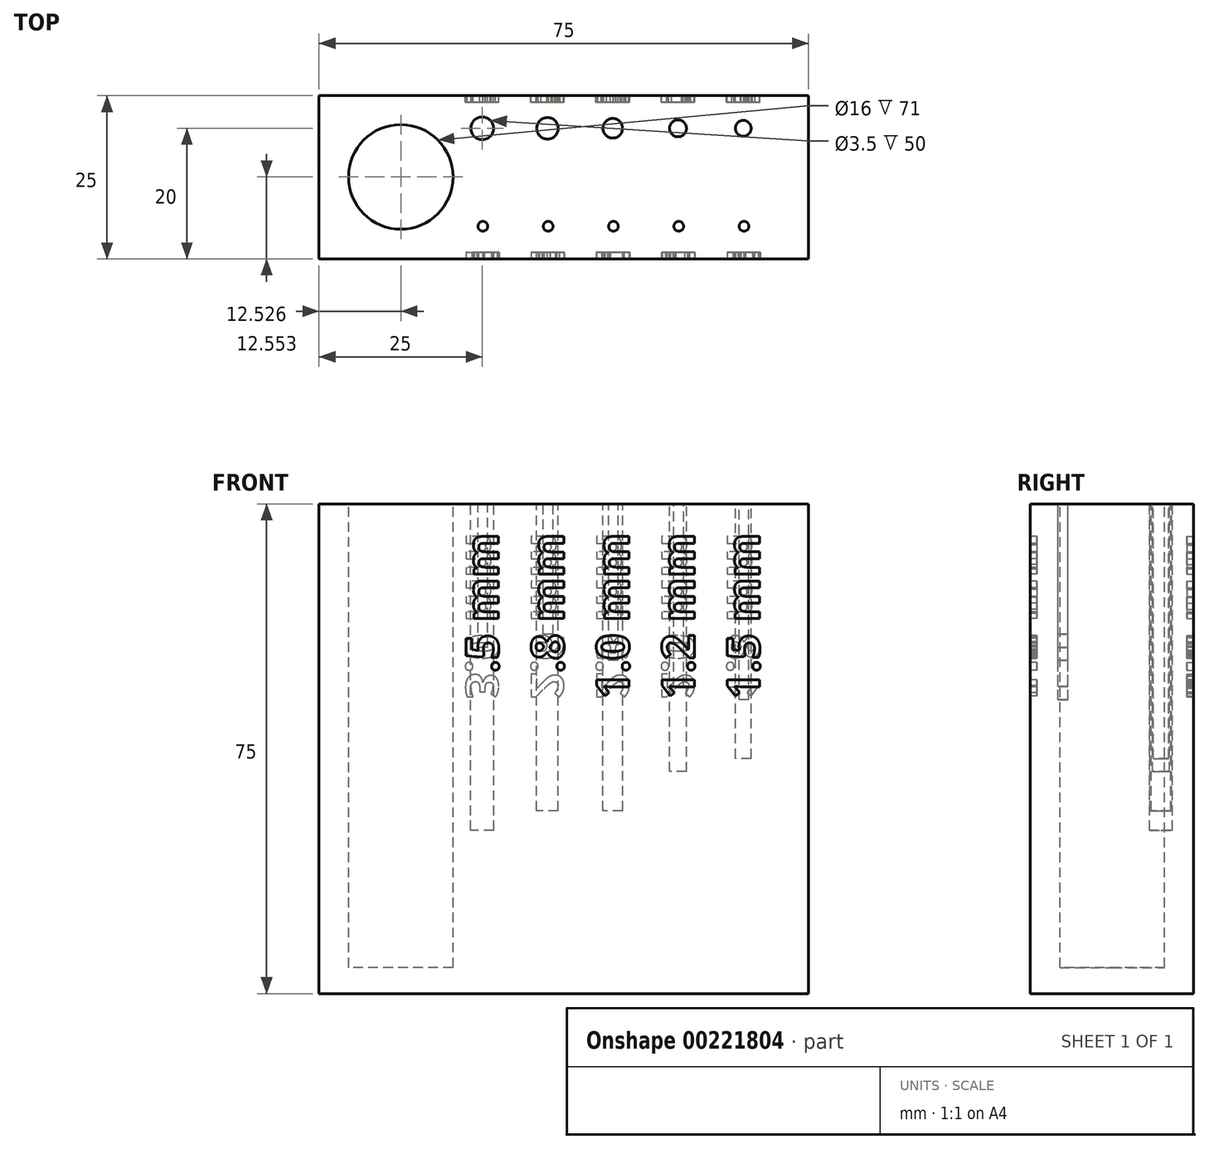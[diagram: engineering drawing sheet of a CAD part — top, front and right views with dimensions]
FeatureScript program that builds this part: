
annotation { "Feature Type Name" : "Feature", "Feature Type Description" : "" }
export const myFeature = defineFeature(function(context is Context, id is Id, definition is map)
    precondition{}
    {
        {
            var Q0;
            Q0=qCreatedBy(makeId("Top.planeOp"),FACE);
            var sketch = newSketch(context, id + "F0", { "sketchPlane" : qUnion([Q0])});
            skLineSegment(sketch, "E0.bottom", {"start": v(-37.5, 12.5) * mm, "end": v(37.5, 12.5) * mm});
            skLineSegment(sketch, "E0.top", {"start": v(-37.5, -12.5) * mm, "end": v(37.5, -12.5) * mm});
            skLineSegment(sketch, "E0.left", {"start": v(-37.5, 12.5) * mm, "end": v(-37.5, -12.5) * mm});
            skLineSegment(sketch, "E0.right", {"start": v(37.5, 12.5) * mm, "end": v(37.5, -12.5) * mm});
            skPoint(sketch, "E0.middle", {"position": v(0, 0) * mm});
            skLineSegment(sketch, "E1", {"start": v(-37.5, 7.5) * mm, "end": v(37.5, 7.5) * mm, "construction": true});
            skPoint(sketch, "E2", {"position": v(27.5, 7.5) * mm});
            skPoint(sketch, "E3.0.1.0", {"position": v(27.6, -7.5) * mm});
            skPoint(sketch, "E3.1.0.0", {"position": v(17.5, 7.5) * mm});
            skPoint(sketch, "E3.1.1.0", {"position": v(17.6, -7.5) * mm});
            skPoint(sketch, "E3.2.0.0", {"position": v(7.5, 7.5) * mm});
            skPoint(sketch, "E3.2.1.0", {"position": v(7.6, -7.5) * mm});
            skPoint(sketch, "E3.3.0.0", {"position": v(-2.5, 7.5) * mm});
            skPoint(sketch, "E3.3.1.0", {"position": v(-2.4, -7.5) * mm});
            skPoint(sketch, "E3.4.0.0", {"position": v(-12.5, 7.5) * mm});
            skPoint(sketch, "E3.4.1.0", {"position": v(-12.4, -7.5) * mm});
            skLineSegment(sketch, "E3.direction1", {"start": v(27.5, 7.5) * mm, "end": v(17.5, 7.5) * mm, "construction": true});
            skLineSegment(sketch, "E3.direction2", {"start": v(27.5, 7.5) * mm, "end": v(27.6, -7.5) * mm, "construction": true});
            skLineSegment(sketch, "E4", {"start": v(-12.5, 12.5) * mm, "end": v(-12.4, -12.5) * mm, "construction": true});
            skPoint(sketch, "E5", {"position": v(-37.5, 0) * mm});
            skLineSegment(sketch, "E6", {"start": v(-37.5, 0) * mm, "end": v(-12.45, 0.1) * mm, "construction": true});
            skPoint(sketch, "E7", {"position": v(-24.97, 0.05) * mm});
            skCircle(sketch, "E8", {"center": v(-24.97, 0.05) * mm, "radius": 8 * mm});
            skCircle(sketch, "E9", {"center": v(-12.4, -7.5) * mm, "radius": 0.75 * mm});
            skCircle(sketch, "E10", {"center": v(-2.4, -7.5) * mm, "radius": 0.75 * mm});
            skCircle(sketch, "E11", {"center": v(7.6, -7.5) * mm, "radius": 0.75 * mm});
            skCircle(sketch, "E12", {"center": v(17.6, -7.5) * mm, "radius": 0.75 * mm});
            skCircle(sketch, "E13", {"center": v(27.6, -7.5) * mm, "radius": 0.75 * mm});
            skCircle(sketch, "E14", {"center": v(27.5, 7.5) * mm, "radius": 1.2 * mm});
            skCircle(sketch, "E15", {"center": v(17.5, 7.5) * mm, "radius": 1.3 * mm});
            skCircle(sketch, "E16", {"center": v(7.5, 7.5) * mm, "radius": 1.5 * mm});
            skCircle(sketch, "E17", {"center": v(-2.5, 7.5) * mm, "radius": 1.65 * mm});
            skCircle(sketch, "E18", {"center": v(-12.5, 7.5) * mm, "radius": 1.75 * mm});
            skSolve(sketch);
        }
        {
            var Q0;
            Q0=makeQuery(id+"F0.imprint","IMPRINT",FACE,{"disambiguationData":[TD([[makeQuery(id+"F0.imprint","IMPRINT",EDGE,{"derivedFrom":sQuery(id+"F0.wireOp",EDGE,"E8")}),1.0]])]});
            var Q1;
            Q1=makeQuery(id+"F0.imprint","IMPRINT",FACE,{"disambiguationData":[TD([[makeQuery(id+"F0.imprint","IMPRINT",EDGE,{"derivedFrom":sQuery(id+"F0.wireOp",EDGE,"E0.bottom")}),-1.0]])]});
            var Q2;
            Q2=makeQuery(id+"F0.imprint","IMPRINT",FACE,{"disambiguationData":[TD([[makeQuery(id+"F0.imprint","IMPRINT",EDGE,{"derivedFrom":sQuery(id+"F0.wireOp",EDGE,"E9")}),1.0]])]});
            var Q3;
            Q3=makeQuery(id+"F0.imprint","IMPRINT",FACE,{"disambiguationData":[TD([[makeQuery(id+"F0.imprint","IMPRINT",EDGE,{"derivedFrom":sQuery(id+"F0.wireOp",EDGE,"E10")}),1.0]])]});
            var Q4;
            Q4=makeQuery(id+"F0.imprint","IMPRINT",FACE,{"disambiguationData":[TD([[makeQuery(id+"F0.imprint","IMPRINT",EDGE,{"derivedFrom":sQuery(id+"F0.wireOp",EDGE,"E11")}),1.0]])]});
            var Q5;
            Q5=makeQuery(id+"F0.imprint","IMPRINT",FACE,{"disambiguationData":[TD([[makeQuery(id+"F0.imprint","IMPRINT",EDGE,{"derivedFrom":sQuery(id+"F0.wireOp",EDGE,"E12")}),1.0]])]});
            var Q6;
            Q6=makeQuery(id+"F0.imprint","IMPRINT",FACE,{"disambiguationData":[TD([[makeQuery(id+"F0.imprint","IMPRINT",EDGE,{"derivedFrom":sQuery(id+"F0.wireOp",EDGE,"E13")}),1.0]])]});
            var Q7;
            Q7=makeQuery(id+"F0.imprint","IMPRINT",FACE,{"disambiguationData":[TD([[makeQuery(id+"F0.imprint","IMPRINT",EDGE,{"derivedFrom":sQuery(id+"F0.wireOp",EDGE,"E14")}),1.0]])]});
            var Q8;
            Q8=makeQuery(id+"F0.imprint","IMPRINT",FACE,{"disambiguationData":[TD([[makeQuery(id+"F0.imprint","IMPRINT",EDGE,{"derivedFrom":sQuery(id+"F0.wireOp",EDGE,"E15")}),1.0]])]});
            var Q9;
            Q9=makeQuery(id+"F0.imprint","IMPRINT",FACE,{"disambiguationData":[TD([[makeQuery(id+"F0.imprint","IMPRINT",EDGE,{"derivedFrom":sQuery(id+"F0.wireOp",EDGE,"E16")}),1.0]])]});
            var Q10;
            Q10=makeQuery(id+"F0.imprint","IMPRINT",FACE,{"disambiguationData":[TD([[makeQuery(id+"F0.imprint","IMPRINT",EDGE,{"derivedFrom":sQuery(id+"F0.wireOp",EDGE,"E17")}),1.0]])]});
            var Q11;
            Q11=makeQuery(id+"F0.imprint","IMPRINT",FACE,{"disambiguationData":[TD([[makeQuery(id+"F0.imprint","IMPRINT",EDGE,{"derivedFrom":sQuery(id+"F0.wireOp",EDGE,"E18")}),1.0]])]});
            extrude(context, id + "F1", {"entities" : qUnion([Q0, Q1, Q2, Q3, Q4, Q5, Q6, Q7, Q8, Q9, Q10, Q11]), "oppositeDirection" : true, "depth" : 75 * mm});
        }
        {
            var Q0;
            Q0=makeQuery(id+"F0.imprint","IMPRINT",FACE,{"disambiguationData":[TD([[makeQuery(id+"F0.imprint","IMPRINT",EDGE,{"derivedFrom":sQuery(id+"F0.wireOp",EDGE,"E8")}),1.0]])]});
            var Q1;
            Q1=sQuery(id+"F0.wireOp",EDGE,"E8");
            extrude(context, id + "F2", {"entities" : qUnion([Q0]), "operationType" : NewBodyOperationType.REMOVE, "surfaceEntities" : qUnion([Q1]), "oppositeDirection" : true, "depth" : 71 * mm});
        }
        {
            var Q0;
            Q0=makeQuery(id+"F0.imprint","IMPRINT",FACE,{"disambiguationData":[TD([[makeQuery(id+"F0.imprint","IMPRINT",EDGE,{"derivedFrom":sQuery(id+"F0.wireOp",EDGE,"E18")}),1.0]])]});
            var Q1;
            Q1=sQuery(id+"F0.wireOp",EDGE,"E18");
            extrude(context, id + "F3", {"entities" : qUnion([Q0]), "operationType" : NewBodyOperationType.REMOVE, "surfaceEntities" : qUnion([Q1]), "oppositeDirection" : true, "depth" : 50 * mm});
        }
        {
            var Q0;
            Q0=makeQuery(id+"F0.imprint","IMPRINT",FACE,{"disambiguationData":[TD([[makeQuery(id+"F0.imprint","IMPRINT",EDGE,{"derivedFrom":sQuery(id+"F0.wireOp",EDGE,"E17")}),1.0]])]});
            extrude(context, id + "F4", {"entities" : qUnion([Q0]), "operationType" : NewBodyOperationType.REMOVE, "oppositeDirection" : true, "depth" : 47 * mm});
        }
        {
            var Q0;
            Q0=makeQuery(id+"F0.imprint","IMPRINT",FACE,{"disambiguationData":[TD([[makeQuery(id+"F0.imprint","IMPRINT",EDGE,{"derivedFrom":sQuery(id+"F0.wireOp",EDGE,"E16")}),1.0]])]});
            extrude(context, id + "F5", {"entities" : qUnion([Q0]), "operationType" : NewBodyOperationType.REMOVE, "oppositeDirection" : true, "depth" : 47 * mm});
        }
        {
            var Q0;
            Q0=makeQuery(id+"F0.imprint","IMPRINT",FACE,{"disambiguationData":[TD([[makeQuery(id+"F0.imprint","IMPRINT",EDGE,{"derivedFrom":sQuery(id+"F0.wireOp",EDGE,"E15")}),1.0]])]});
            extrude(context, id + "F6", {"entities" : qUnion([Q0]), "operationType" : NewBodyOperationType.REMOVE, "oppositeDirection" : true, "depth" : 41 * mm});
        }
        {
            var Q0;
            Q0=makeQuery(id+"F0.imprint","IMPRINT",FACE,{"disambiguationData":[TD([[makeQuery(id+"F0.imprint","IMPRINT",EDGE,{"derivedFrom":sQuery(id+"F0.wireOp",EDGE,"E14")}),1.0]])]});
            extrude(context, id + "F7", {"entities" : qUnion([Q0]), "operationType" : NewBodyOperationType.REMOVE, "oppositeDirection" : true, "depth" : 39 * mm});
        }
        {
            var Q0;
            Q0=makeQuery(id+"F0.imprint","IMPRINT",FACE,{"disambiguationData":[TD([[makeQuery(id+"F0.imprint","IMPRINT",EDGE,{"derivedFrom":sQuery(id+"F0.wireOp",EDGE,"E13")}),1.0]])]});
            extrude(context, id + "F8", {"entities" : qUnion([Q0]), "operationType" : NewBodyOperationType.REMOVE, "oppositeDirection" : true, "depth" : 30 * mm});
        }
        {
            var Q0;
            Q0=makeQuery(id+"F0.imprint","IMPRINT",FACE,{"disambiguationData":[TD([[makeQuery(id+"F0.imprint","IMPRINT",EDGE,{"derivedFrom":sQuery(id+"F0.wireOp",EDGE,"E12")}),1.0]])]});
            extrude(context, id + "F9", {"entities" : qUnion([Q0]), "operationType" : NewBodyOperationType.REMOVE, "oppositeDirection" : true, "depth" : 28 * mm});
        }
        {
            var Q0;
            Q0=makeQuery(id+"F0.imprint","IMPRINT",FACE,{"disambiguationData":[TD([[makeQuery(id+"F0.imprint","IMPRINT",EDGE,{"derivedFrom":sQuery(id+"F0.wireOp",EDGE,"E11")}),1.0]])]});
            extrude(context, id + "F10", {"entities" : qUnion([Q0]), "operationType" : NewBodyOperationType.REMOVE, "oppositeDirection" : true, "depth" : 24 * mm});
        }
        {
            var Q0;
            Q0=makeQuery(id+"F0.imprint","IMPRINT",FACE,{"disambiguationData":[TD([[makeQuery(id+"F0.imprint","IMPRINT",EDGE,{"derivedFrom":sQuery(id+"F0.wireOp",EDGE,"E10")}),1.0]])]});
            extrude(context, id + "F11", {"entities" : qUnion([Q0]), "operationType" : NewBodyOperationType.REMOVE, "oppositeDirection" : true, "depth" : 20 * mm});
        }
        {
            var Q0;
            Q0=makeQuery(id+"F0.imprint","IMPRINT",FACE,{"disambiguationData":[TD([[makeQuery(id+"F0.imprint","IMPRINT",EDGE,{"derivedFrom":sQuery(id+"F0.wireOp",EDGE,"E9")}),1.0]])]});
            extrude(context, id + "F12", {"entities" : qUnion([Q0]), "operationType" : NewBodyOperationType.REMOVE, "oppositeDirection" : true, "depth" : 22 * mm});
        }
        {
            var Q0;
            Q0=makeQuery(id+"F1.opExtrude","SWEPT_FACE",FACE,{"disambiguationData":[OSD([sQuery(id+"F0.wireOp",EDGE,"E0.top")])]});
            var sketch = newSketch(context, id + "F13", { "sketchPlane" : qUnion([Q0])});
            skLineSegment(sketch, "E19.0", {"start": v(-14.25, 0) * mm, "end": v(-10.75, 0) * mm});
            skLineSegment(sketch, "E20.0", {"start": v(-4.15, 0) * mm, "end": v(-0.85, 0) * mm});
            skLineSegment(sketch, "E21.0", {"start": v(6, 0) * mm, "end": v(9, 0) * mm});
            skLineSegment(sketch, "E22.0", {"start": v(16.2, 0) * mm, "end": v(18.8, 0) * mm});
            skLineSegment(sketch, "E23.0", {"start": v(26.3, 0) * mm, "end": v(28.7, 0) * mm});
            skLineSegment(sketch, "E24", {"start": v(-12.5, 0) * mm, "end": v(-12.5, -75) * mm, "construction": true});
            skLineSegment(sketch, "E25", {"start": v(-2.5, 0) * mm, "end": v(-2.5, -75) * mm, "construction": true});
            skLineSegment(sketch, "E26", {"start": v(7.5, 0) * mm, "end": v(7.5, -75) * mm, "construction": true});
            skLineSegment(sketch, "E27", {"start": v(17.5, 0) * mm, "end": v(17.5, -75) * mm, "construction": true});
            skLineSegment(sketch, "E28", {"start": v(27.5, 0) * mm, "end": v(27.5, -75) * mm, "construction": true});
            skText(sketch, "E29", { "text": ".5 mm", "fontName": "OpenSans-Bold.ttf"});
            skLineSegment(sketch, "E30", {"start": v(-37.5, -5) * mm, "end": v(37.5, -5) * mm, "construction": true});
            skLineSegment(sketch, "E31", {"start": v(-12.5, -5) * mm, "end": v(-12.5, -25.87) * mm, "construction": true});
            skText(sketch, "E32", { "text": ".8 mm", "fontName": "OpenSans-Bold.ttf"});
            skLineSegment(sketch, "E33", {"start": v(-23.37, -5) * mm, "end": v(-2.5, -5) * mm, "construction": true});
            skPoint(sketch, "E34", {"position": v(-2.5, -5) * mm});
            skPoint(sketch, "E35", {"position": v(7.5, -5) * mm});
            skPoint(sketch, "E36", {"position": v(17.5, -5) * mm});
            skPoint(sketch, "E37", {"position": v(27.5, -5) * mm});
            skLineSegment(sketch, "E38", {"start": v(-2.5, -25.87) * mm, "end": v(-2.5, -5) * mm, "construction": true});
            skText(sketch, "E39", { "text": "1.0 mm", "fontName": "OpenSans-Bold.ttf"});
            skText(sketch, "E40", { "text": "1.2 mm", "fontName": "OpenSans-Bold.ttf"});
            skText(sketch, "E41", { "text": "1.5 mm", "fontName": "OpenSans-Bold.ttf"});
            skLineSegment(sketch, "E42", {"start": v(7.5, -29.83) * mm, "end": v(7.5, -5) * mm, "construction": true});
            skLineSegment(sketch, "E43", {"start": v(17.5, -29.83) * mm, "end": v(17.5, -5) * mm, "construction": true});
            skLineSegment(sketch, "E44", {"start": v(27.5, -29.83) * mm, "end": v(27.5, -5) * mm, "construction": true});
            const initialGuessF13  = {"E29": [-0.01, -0.02587, 0, 1, 0.005], "E32": [0, -0.02587, 0, 1, 0.005], "E39": [0.01, -0.02983, 0, 1, 0.005], "E40": [0.02, -0.02983, 0, 1, 0.005], "E41": [0.03, -0.02983, 0, 1, 0.005]};
            skSetInitialGuess(sketch, initialGuessF13);
            skSolve(sketch);
        }
        {
            var Q0;
            Q0=qSketchRegion(id+"F13",true);
            extrude(context, id + "F14", {"entities" : qUnion([Q0]), "operationType" : NewBodyOperationType.REMOVE, "oppositeDirection" : true, "depth" : 1 * mm});
        }
        {
            var Q0;
            Q0=makeQuery(id+"F1.opExtrude","SWEPT_FACE",FACE,{"disambiguationData":[OSD([sQuery(id+"F0.wireOp",EDGE,"E0.bottom")])]});
            var sketch = newSketch(context, id + "F15", { "sketchPlane" : qUnion([Q0])});
            skLineSegment(sketch, "E45.0", {"start": v(37.5, -5) * mm, "end": v(-37.5, -5) * mm, "construction": true});
            skLineSegment(sketch, "E46.0", {"start": v(12.5, 0) * mm, "end": v(12.5, -75) * mm, "construction": true});
            skLineSegment(sketch, "E46.1", {"start": v(2.5, 0) * mm, "end": v(2.5, -75) * mm, "construction": true});
            skLineSegment(sketch, "E46.2", {"start": v(-7.5, 0) * mm, "end": v(-7.5, -75) * mm, "construction": true});
            skLineSegment(sketch, "E46.3", {"start": v(-17.5, 0) * mm, "end": v(-17.5, -75) * mm, "construction": true});
            skLineSegment(sketch, "E46.4", {"start": v(-27.5, 0) * mm, "end": v(-27.5, -75) * mm, "construction": true});
            skText(sketch, "E47", { "text": "1.8 mm", "fontName": "OpenSans-Bold.ttf"});
            skText(sketch, "E48", { "text": "2.0 mm", "fontName": "OpenSans-Bold.ttf"});
            skText(sketch, "E49", { "text": "2.3 mm", "fontName": "OpenSans-Bold.ttf"});
            skText(sketch, "E50", { "text": "2.6 mm", "fontName": "OpenSans-Bold.ttf"});
            skText(sketch, "E51", { "text": "3.0 mm", "fontName": "OpenSans-Bold.ttf"});
            skLineSegment(sketch, "E52", {"start": v(-27.5, -29.83) * mm, "end": v(-27.5, -5) * mm, "construction": true});
            skLineSegment(sketch, "E53", {"start": v(-17.5, -29.83) * mm, "end": v(-17.5, -5) * mm, "construction": true});
            skLineSegment(sketch, "E54", {"start": v(-7.5, -29.83) * mm, "end": v(-7.5, -5) * mm, "construction": true});
            skLineSegment(sketch, "E55", {"start": v(2.5, -29.83) * mm, "end": v(2.5, -5) * mm, "construction": true});
            skLineSegment(sketch, "E56", {"start": v(12.5, -29.83) * mm, "end": v(12.5, -5) * mm, "construction": true});
            skPoint(sketch, "E57", {"position": v(-27.5, -5) * mm});
            skPoint(sketch, "E58", {"position": v(-17.5, -5) * mm});
            skPoint(sketch, "E59", {"position": v(-7.5, -5) * mm});
            skPoint(sketch, "E60", {"position": v(2.5, -5) * mm});
            skPoint(sketch, "E61", {"position": v(12.5, -5) * mm});
            const initialGuessF15  = {"E47": [-0.025, -0.02983, 0, 1, 0.005], "E48": [-0.015, -0.02983, 0, 1, 0.005], "E49": [-0.005, -0.02983, 0, 1, 0.005], "E50": [0.005, -0.02983, 0, 1, 0.005], "E51": [0.015, -0.02983, 0, 1, 0.005]};
            skSetInitialGuess(sketch, initialGuessF15);
            skSolve(sketch);
        }
        {
            var Q0;
            Q0=qSketchRegion(id+"F15",true);
            extrude(context, id + "F16", {"entities" : qUnion([Q0]), "operationType" : NewBodyOperationType.REMOVE, "oppositeDirection" : true, "depth" : 1 * mm});
        }
    });
